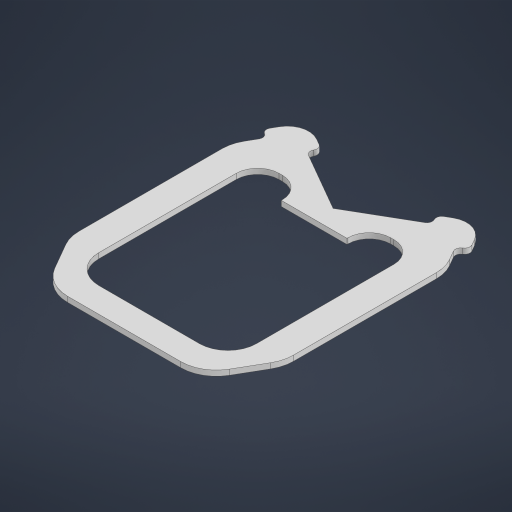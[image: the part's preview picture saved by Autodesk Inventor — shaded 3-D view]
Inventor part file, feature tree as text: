
AUTODESK INVENTOR PART (.ipt)
format: ipt  version: 2023 (Build 270158000, 158)  size: 459,264 bytes
history: native  units: in
note: dims shown in document units (in); Inventor stores cm internally (conversion verified against a paired STEP export)
features: extrude x8, chamfer x4, sketch x3, fillet x2, draft x1, direct_edit x1, move_body x1
ambient origin geometry x8: Origin, YZ Plane, XZ Plane, XY Plane, X Axis, Y Axis, Z Axis, Center Point
bodies: Solid1 (feature_tree)
feature tree (20):
  extrude  "Extrusion1"  Depth=0.1181in
  extrude  "Extrusion2"  Depth=0.3937in TaperAngle=0.0deg
  extrude  "Extrusion3"  Depth=0.1181in
  extrude  "Extrusion4"  Depth=0.315in
  extrude  "Extrusion5"  Depth=0.2362in
  chamfer  "Chamfer1"  Distance=0.2362in
  chamfer  "Chamfer2"  Distance=0.5689in
  chamfer  "Chamfer3"  Distance=0.0787in
  sketch  "Sketch2"  dims[d1=0.374in d3=120.0deg d4=60.0deg d5=0.1772in d6=2.9528in d11=0.0886in d14=60.0deg d15=0.1772in d16=0.0886in d17=1.5748in d18=0.1181in]
  fillet  "Fillet3"  Radius=0.0787in
  extrude  "Extrusion7"  Depth=0.315in
  draft  "FaceDraft3"
  fillet  "Fillet10"  Radius=0.0197in
  chamfer  "Chamfer8"  Distance=0.0394in
  extrude  "Extrusion10"  Depth=0.2362in
  sketch  "Sketch8"  dims[d22=0.2657in d24=0.1181in d25=0.315in d26=0.2362in d27=0.2362in d28=0.5689in d29=0.0787in d30=0.0787in d31=0.0787in d32=0.0197in d33=0.0in d34=0.0394in d35=0.0in d36=0.2362in d37=0.0in d38=0.0in d39=0.0in d40=0.0in d41=0.0in d42=0.0591in d43=0.2362in d44=0.0in d45=0.2756in d46=0.0492in d47=0.0in d48=0.2756in d49=0.0098in d50=45.0deg d52=0.0394in d53=0.1575in d54=75.0deg d55=0.0394in d56=0.1575in d57=75.0deg d66=0.315in d67=0.3937in d72=0.1575in d73=0.0in d74=45.0deg d105=0.315in d106=0.0787in d107=0.0787in d108=0.2405in d109=0.0787in d110=0.0in d111=0.0in d112=0.0in d113=0.1378in d114=0.0in d115=0.0in d51=0.0in d59=0.0in d60=0.0in d61=0.0in d62=0.0in d63=0.0in d64=0.0in d65=0.0in d68=0.0344in d69=0.0197in d70=0.0344in d104=0.0in]
  direct_edit  "Direct Edit3"
  extrude  "Extrusion11"  TaperAngle=0.0deg  [1 undecoded]
  sketch  "Sketch7"  dims[d19=0.3937in d20=0.1969in d21=0.0in]
  move_body  "Move5"
note: 1 required parameter value undecoded (feature->parameter linkage not recoverable at this tier; creation-order binding heuristic only, values carry confidence <= 0.55)
